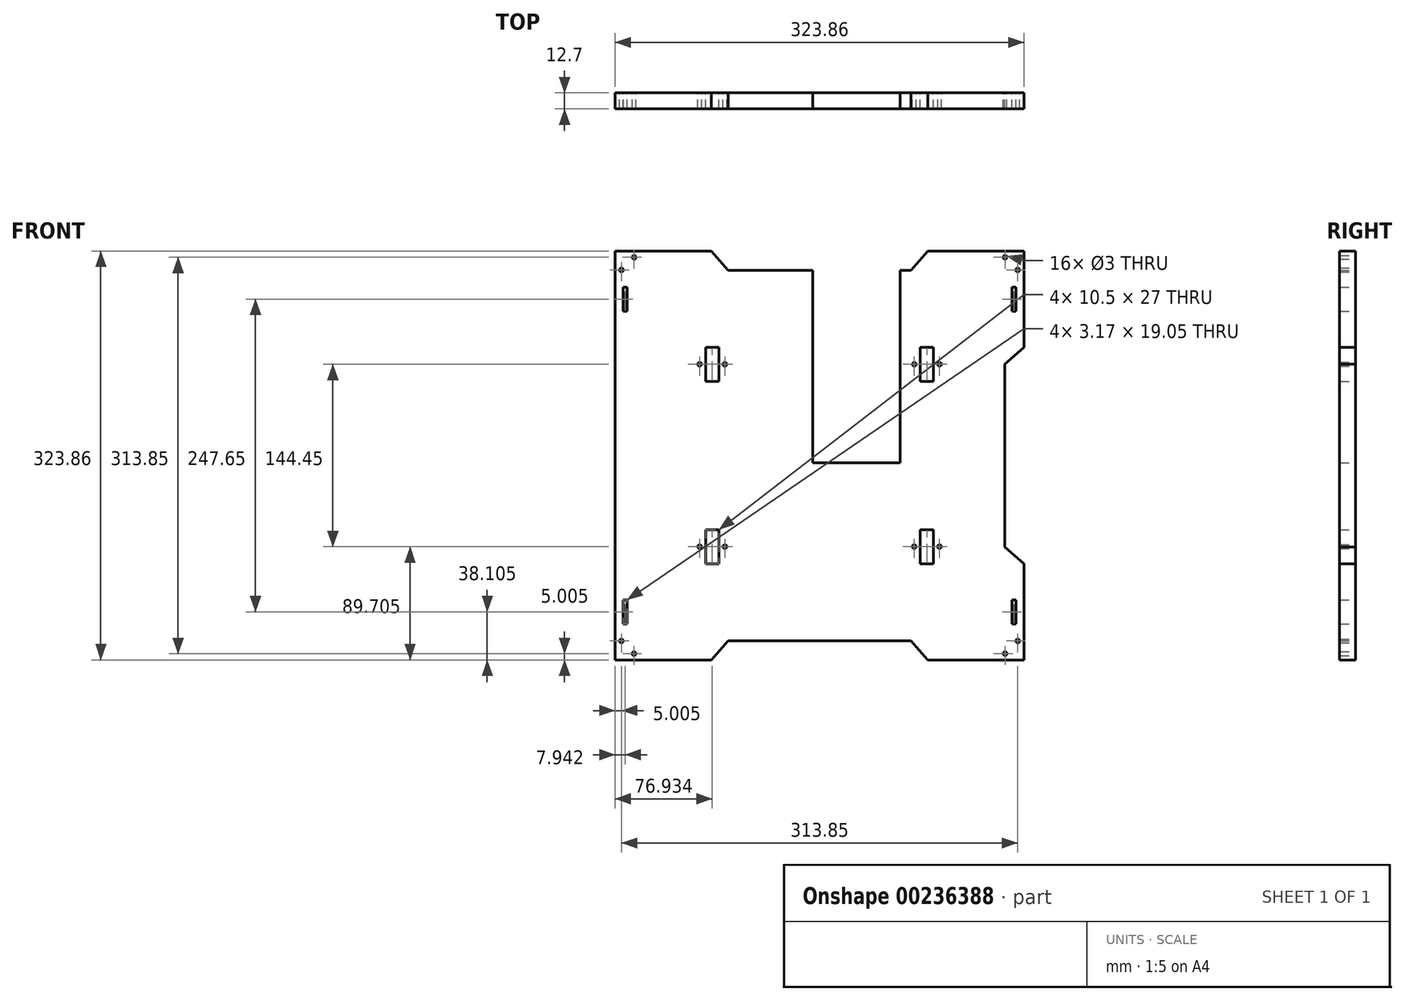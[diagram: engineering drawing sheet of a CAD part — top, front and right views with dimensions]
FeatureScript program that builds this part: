
annotation { "Feature Type Name" : "Feature", "Feature Type Description" : "" }
export const myFeature = defineFeature(function(context is Context, id is Id, definition is map)
    precondition{}
    {
        {
            var Q0;
            Q0=qCreatedBy(makeId("Front.planeOp"),FACE);
            var sketch = newSketch(context, id + "F0", { "sketchPlane" : qUnion([Q0])});
            skLineSegment(sketch, "E0.bottom", {"start": v(-161.93, 161.93) * mm, "end": v(-85.73, 161.93) * mm});
            skLineSegment(sketch, "E0.top", {"start": v(-161.93, -161.93) * mm, "end": v(-85.73, -161.93) * mm});
            skLineSegment(sketch, "E0.left", {"start": v(-161.93, 161.93) * mm, "end": v(-161.93, -161.93) * mm});
            skLineSegment(sketch, "E0.right", {"start": v(161.93, 161.93) * mm, "end": v(161.93, 85.73) * mm});
            skLineSegment(sketch, "E1.bottom", {"start": v(-90.25, -58.73) * mm, "end": v(-79.75, -58.73) * mm});
            skLineSegment(sketch, "E1.top", {"start": v(-90.25, -85.73) * mm, "end": v(-79.75, -85.73) * mm});
            skLineSegment(sketch, "E1.left", {"start": v(-90.25, -58.73) * mm, "end": v(-90.25, -85.73) * mm});
            skLineSegment(sketch, "E1.right", {"start": v(-79.75, -58.73) * mm, "end": v(-79.75, -85.73) * mm});
            skLineSegment(sketch, "E2.bottom", {"start": v(79.75, -58.73) * mm, "end": v(90.25, -58.73) * mm});
            skLineSegment(sketch, "E2.top", {"start": v(79.75, -85.73) * mm, "end": v(90.25, -85.73) * mm});
            skLineSegment(sketch, "E2.left", {"start": v(79.75, -58.73) * mm, "end": v(79.75, -85.73) * mm});
            skLineSegment(sketch, "E2.right", {"start": v(90.25, -58.73) * mm, "end": v(90.25, -85.73) * mm});
            skLineSegment(sketch, "E3.bottom", {"start": v(-90.25, 85.72) * mm, "end": v(-79.75, 85.72) * mm});
            skLineSegment(sketch, "E3.top", {"start": v(-90.25, 58.72) * mm, "end": v(-79.75, 58.72) * mm});
            skLineSegment(sketch, "E3.left", {"start": v(-90.25, 85.73) * mm, "end": v(-90.25, 58.73) * mm});
            skLineSegment(sketch, "E3.right", {"start": v(-79.75, 85.73) * mm, "end": v(-79.75, 58.73) * mm});
            skLineSegment(sketch, "E4.bottom", {"start": v(79.75, 85.73) * mm, "end": v(90.25, 85.73) * mm});
            skLineSegment(sketch, "E4.top", {"start": v(79.75, 58.73) * mm, "end": v(90.25, 58.73) * mm});
            skLineSegment(sketch, "E4.left", {"start": v(79.75, 85.73) * mm, "end": v(79.75, 58.73) * mm});
            skLineSegment(sketch, "E4.right", {"start": v(90.25, 85.73) * mm, "end": v(90.25, 58.73) * mm});
            skCircle(sketch, "E5", {"center": v(75, -72.23) * mm, "radius": 1.5 * mm});
            skPoint(sketch, "E5.centerSnap0", {"position": v(79.75, -72.23) * mm});
            skCircle(sketch, "E6", {"center": v(95, -72.23) * mm, "radius": 1.5 * mm});
            skCircle(sketch, "E7", {"center": v(75, 72.23) * mm, "radius": 1.5 * mm});
            skPoint(sketch, "E7.centerSnap0", {"position": v(79.75, 72.23) * mm});
            skCircle(sketch, "E8", {"center": v(95, 72.23) * mm, "radius": 1.5 * mm});
            skPoint(sketch, "E8.centerSnap0", {"position": v(90.25, 72.23) * mm});
            skCircle(sketch, "E9", {"center": v(-75, 72.23) * mm, "radius": 1.5 * mm});
            skPoint(sketch, "E9.centerSnap0", {"position": v(-79.75, 72.23) * mm});
            skCircle(sketch, "E10", {"center": v(-95, 72.23) * mm, "radius": 1.5 * mm});
            skPoint(sketch, "E10.centerSnap0", {"position": v(-90.25, 72.23) * mm});
            skCircle(sketch, "E11", {"center": v(-95, -72.23) * mm, "radius": 1.5 * mm});
            skPoint(sketch, "E11.centerSnap0", {"position": v(-90.25, -72.23) * mm});
            skCircle(sketch, "E12", {"center": v(-75, -72.23) * mm, "radius": 1.5 * mm});
            skPoint(sketch, "E12.centerSnap0", {"position": v(-79.75, -72.23) * mm});
            skLineSegment(sketch, "E13", {"start": v(-85.72, -161.93) * mm, "end": v(-72.43, -146.69) * mm});
            skLineSegment(sketch, "E14", {"start": v(-72.43, -146.69) * mm, "end": v(72.43, -146.69) * mm});
            skLineSegment(sketch, "E15", {"start": v(72.43, -146.69) * mm, "end": v(85.73, -161.92) * mm});
            skLineSegment(sketch, "E16", {"start": v(-85.73, 161.92) * mm, "end": v(-72.43, 146.69) * mm});
            skLineSegment(sketch, "E17", {"start": v(-72.43, 146.69) * mm, "end": v(-5.25, 146.69) * mm});
            skLineSegment(sketch, "E18", {"start": v(72.43, 146.68) * mm, "end": v(85.73, 161.93) * mm});
            skLineSegment(sketch, "E19", {"start": v(161.93, 85.73) * mm, "end": v(146.69, 72.43) * mm});
            skLineSegment(sketch, "E20", {"start": v(146.69, 72.43) * mm, "end": v(146.69, -72.43) * mm});
            skLineSegment(sketch, "E21", {"start": v(146.69, -72.43) * mm, "end": v(161.93, -85.72) * mm});
            skLineSegment(sketch, "E22", {"start": v(-161.93, 85.73) * mm, "end": v(-146.69, 72.43) * mm});
            skLineSegment(sketch, "E23", {"start": v(-146.69, 72.43) * mm, "end": v(-146.69, -72.43) * mm});
            skLineSegment(sketch, "E24", {"start": v(-146.69, -72.43) * mm, "end": v(-161.93, -85.73) * mm});
            skLineSegment(sketch, "E25.bottom", {"start": v(-155.58, 133.35) * mm, "end": v(-152.4, 133.35) * mm});
            skLineSegment(sketch, "E25.top", {"start": v(-155.58, 114.3) * mm, "end": v(-152.4, 114.3) * mm});
            skLineSegment(sketch, "E25.left", {"start": v(-155.58, 133.35) * mm, "end": v(-155.58, 114.3) * mm});
            skLineSegment(sketch, "E25.right", {"start": v(-152.4, 133.35) * mm, "end": v(-152.4, 114.3) * mm});
            skLineSegment(sketch, "E26.bottom", {"start": v(-155.58, -114.3) * mm, "end": v(-152.4, -114.3) * mm});
            skLineSegment(sketch, "E26.top", {"start": v(-155.58, -133.35) * mm, "end": v(-152.4, -133.35) * mm});
            skLineSegment(sketch, "E26.left", {"start": v(-155.58, -114.3) * mm, "end": v(-155.58, -133.35) * mm});
            skLineSegment(sketch, "E26.right", {"start": v(-152.4, -114.3) * mm, "end": v(-152.4, -133.35) * mm});
            skLineSegment(sketch, "E27.bottom", {"start": v(152.4, -114.3) * mm, "end": v(155.58, -114.3) * mm});
            skLineSegment(sketch, "E27.top", {"start": v(152.4, -133.35) * mm, "end": v(155.58, -133.35) * mm});
            skLineSegment(sketch, "E27.left", {"start": v(152.4, -114.3) * mm, "end": v(152.4, -133.35) * mm});
            skLineSegment(sketch, "E27.right", {"start": v(155.58, -114.3) * mm, "end": v(155.58, -133.35) * mm});
            skLineSegment(sketch, "E28.bottom", {"start": v(152.4, 133.35) * mm, "end": v(155.58, 133.35) * mm});
            skLineSegment(sketch, "E28.top", {"start": v(152.4, 114.3) * mm, "end": v(155.58, 114.3) * mm});
            skLineSegment(sketch, "E28.left", {"start": v(152.4, 133.35) * mm, "end": v(152.4, 114.3) * mm});
            skLineSegment(sketch, "E28.right", {"start": v(155.58, 133.35) * mm, "end": v(155.58, 114.3) * mm});
            skLineSegment(sketch, "E29.trimOffspring", {"start": v(161.93, -85.72) * mm, "end": v(161.93, -161.93) * mm});
            skLineSegment(sketch, "E30.trimOffspring", {"start": v(85.73, 161.93) * mm, "end": v(161.93, 161.93) * mm});
            skLineSegment(sketch, "E31.trimOffspring", {"start": v(85.73, -161.93) * mm, "end": v(161.93, -161.93) * mm});
            skCircle(sketch, "E32", {"center": v(-156.93, -146.93) * mm, "radius": 1.5 * mm});
            skCircle(sketch, "E33", {"center": v(-146.93, -156.93) * mm, "radius": 1.5 * mm});
            skCircle(sketch, "E34", {"center": v(146.93, -156.93) * mm, "radius": 1.5 * mm});
            skCircle(sketch, "E35", {"center": v(156.93, -146.93) * mm, "radius": 1.5 * mm});
            skCircle(sketch, "E36", {"center": v(146.93, 156.93) * mm, "radius": 1.5 * mm});
            skCircle(sketch, "E37", {"center": v(156.92, 146.93) * mm, "radius": 1.5 * mm});
            skCircle(sketch, "E38", {"center": v(-146.93, 156.93) * mm, "radius": 1.5 * mm});
            skCircle(sketch, "E39", {"center": v(-156.93, 146.93) * mm, "radius": 1.5 * mm});
            skLineSegment(sketch, "E40", {"start": v(63.75, 146.69) * mm, "end": v(63.75, -5.71) * mm});
            skLineSegment(sketch, "E41", {"start": v(63.75, -5.71) * mm, "end": v(-5.25, -5.71) * mm});
            skLineSegment(sketch, "E42", {"start": v(-5.25, -5.71) * mm, "end": v(-5.25, 146.69) * mm});
            skLineSegment(sketch, "E43.trimOffspring", {"start": v(63.75, 146.69) * mm, "end": v(72.43, 146.69) * mm});
            skSolve(sketch);
        }
        {
            var Q0;
            Q0 = qSketchRegion(id + "F0", true);
            extrude(context, id + "F1", {"entities" : qUnion([Q0]), "depth" : 12.7 * mm});
        }
    });
